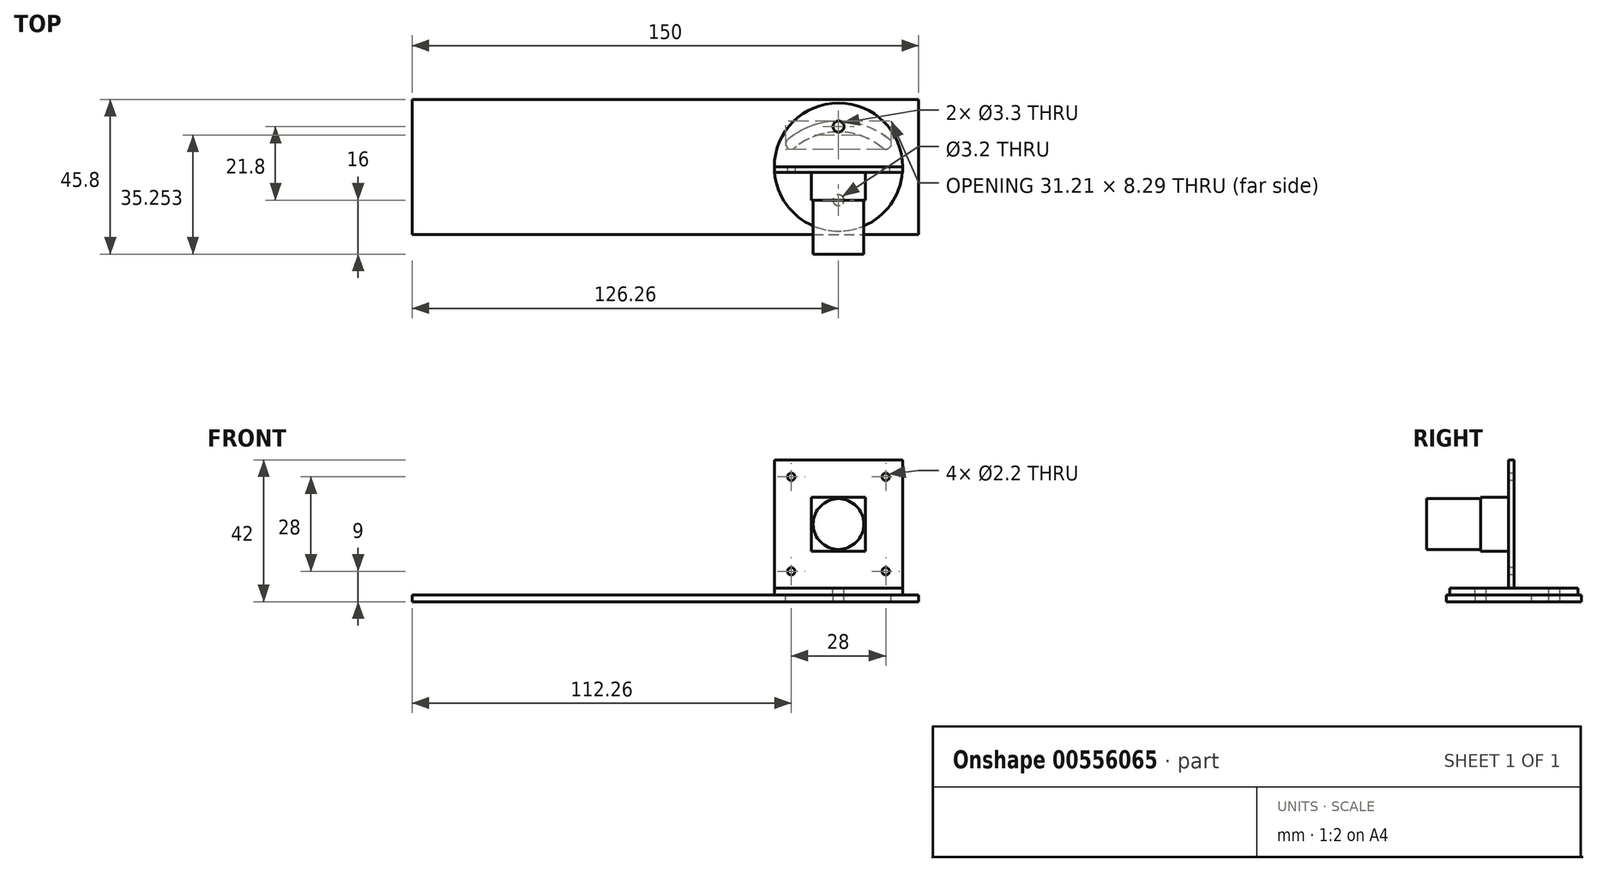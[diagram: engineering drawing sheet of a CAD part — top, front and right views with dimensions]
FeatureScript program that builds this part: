
annotation { "Feature Type Name" : "Feature", "Feature Type Description" : "" }
export const myFeature = defineFeature(function(context is Context, id is Id, definition is map)
    precondition{}
    {
        {
            var Q0;
            Q0=qCreatedBy(makeId("Front.planeOp"),FACE);
            var sketch = newSketch(context, id + "F0", { "sketchPlane" : qUnion([Q0])});
            skLineSegment(sketch, "E0.bottom", {"start": v(19, -19) * mm, "end": v(-19, -19) * mm});
            skLineSegment(sketch, "E0.top", {"start": v(19, 19) * mm, "end": v(-19, 19) * mm});
            skLineSegment(sketch, "E0.left", {"start": v(19, -19) * mm, "end": v(19, 19) * mm});
            skLineSegment(sketch, "E0.right", {"start": v(-19, -19) * mm, "end": v(-19, 19) * mm});
            skPoint(sketch, "E0.middle", {"position": v(0, 0) * mm});
            skSolve(sketch);
        }
        {
            var Q0;
            Q0 = qSketchRegion(id + "F0", true);
            extrude(context, id + "F1", {"entities" : qUnion([Q0]), "depth" : 1.6 * mm, "offsetDistance" : 25 * mm});
        }
        {
            var Q0;
            Q0=makeQuery(id+"F1.opExtrude","CAP_FACE",FACE,{"disambiguationData":[OSD([sQuery(id+"F0.wireOp",EDGE,"E0.bottom"),sQuery(id+"F0.wireOp",EDGE,"E0.top"),sQuery(id+"F0.wireOp",EDGE,"E0.left"),sQuery(id+"F0.wireOp",EDGE,"E0.right")])],"isStart":false});
            var sketch = newSketch(context, id + "F2", { "sketchPlane" : qUnion([Q0])});
            skLineSegment(sketch, "E1.bottom", {"start": v(14, -14) * mm, "end": v(-14, -14) * mm, "construction": true});
            skLineSegment(sketch, "E1.top", {"start": v(14, 14) * mm, "end": v(-14, 14) * mm, "construction": true});
            skLineSegment(sketch, "E1.left", {"start": v(14, -14) * mm, "end": v(14, 14) * mm, "construction": true});
            skLineSegment(sketch, "E1.right", {"start": v(-14, -14) * mm, "end": v(-14, 14) * mm, "construction": true});
            skPoint(sketch, "E1.middle", {"position": v(0, 0) * mm});
            skCircle(sketch, "E2", {"center": v(-14, 14) * mm, "radius": 1.1 * mm});
            skLineSegment(sketch, "E3", {"start": v(0, 19) * mm, "end": v(0, -19) * mm, "construction": true});
            skLineSegment(sketch, "E4", {"start": v(-19, 0) * mm, "end": v(19, 0) * mm, "construction": true});
            skCircle(sketch, "E5.MirrorC", {"center": v(14, 14) * mm, "radius": 1.1 * mm});
            skCircle(sketch, "E6.MirrorC", {"center": v(-14, -14) * mm, "radius": 1.1 * mm});
            skCircle(sketch, "E7.MirrorC", {"center": v(14, -14) * mm, "radius": 1.1 * mm});
            skSolve(sketch);
        }
        {
            var Q0;
            Q0 = qSketchRegion(id + "F2", true);
            var Q1;
            Q1=makeQuery(id+"F1.opExtrude","CAP_FACE",FACE,{"disambiguationData":[OSD([sQuery(id+"F0.wireOp",EDGE,"E0.bottom"),sQuery(id+"F0.wireOp",EDGE,"E0.top"),sQuery(id+"F0.wireOp",EDGE,"E0.left"),sQuery(id+"F0.wireOp",EDGE,"E0.right")])],"isStart":true});
            extrude(context, id + "F3", {"entities" : qUnion([Q0]), "operationType" : NewBodyOperationType.REMOVE, "endBound" : BoundingType.UP_TO_SURFACE, "oppositeDirection" : true, "depth" : 25 * mm, "endBoundEntityFace" : qUnion([Q1]), "offsetDistance" : 25 * mm});
        }
        {
            var Q0;
            Q0=makeQuery(id+"F1.opExtrude","CAP_FACE",FACE,{"disambiguationData":[OSD([sQuery(id+"F0.wireOp",EDGE,"E0.bottom"),sQuery(id+"F0.wireOp",EDGE,"E0.top"),sQuery(id+"F0.wireOp",EDGE,"E0.left"),sQuery(id+"F0.wireOp",EDGE,"E0.right")])],"isStart":false});
            var sketch = newSketch(context, id + "F4", { "sketchPlane" : qUnion([Q0])});
            skLineSegment(sketch, "E8.bottom", {"start": v(8, -8) * mm, "end": v(-8, -8) * mm});
            skLineSegment(sketch, "E8.top", {"start": v(8, 8) * mm, "end": v(-8, 8) * mm});
            skLineSegment(sketch, "E8.left", {"start": v(8, -8) * mm, "end": v(8, 8) * mm});
            skLineSegment(sketch, "E8.right", {"start": v(-8, -8) * mm, "end": v(-8, 8) * mm});
            skPoint(sketch, "E8.middle", {"position": v(0, 0) * mm});
            skSolve(sketch);
        }
        {
            var Q0;
            Q0 = qSketchRegion(id + "F4", true);
            extrude(context, id + "F5", {"entities" : qUnion([Q0]), "operationType" : NewBodyOperationType.ADD, "depth" : 8.2 * mm, "offsetDistance" : 25 * mm});
        }
        {
            var Q0;
            Q0=makeQuery(id+"F5.opExtrude","CAP_FACE",FACE,{"disambiguationData":[OSD([sQuery(id+"F4.wireOp",EDGE,"E8.bottom"),sQuery(id+"F4.wireOp",EDGE,"E8.top"),sQuery(id+"F4.wireOp",EDGE,"E8.left"),sQuery(id+"F4.wireOp",EDGE,"E8.right")])],"isStart":false});
            var sketch = newSketch(context, id + "F6", { "sketchPlane" : qUnion([Q0])});
            skLineSegment(sketch, "E9", {"start": v(0, 8) * mm, "end": v(0, -8) * mm, "construction": true});
            skLineSegment(sketch, "E10", {"start": v(-8, 0) * mm, "end": v(8, 0) * mm, "construction": true});
            skCircle(sketch, "E11", {"center": v(0, 0) * mm, "radius": 7.5 * mm});
            skSolve(sketch);
        }
        {
            var Q0;
            Q0 = qSketchRegion(id + "F6", true);
            extrude(context, id + "F7", {"entities" : qUnion([Q0]), "operationType" : NewBodyOperationType.ADD, "depth" : 16 * mm, "offsetDistance" : 25 * mm});
        }
        {
            var Q0;
            Q0=makeQuery(id+"F1.opExtrude","SWEPT_FACE",FACE,{"disambiguationData":[OSD([sQuery(id+"F0.wireOp",EDGE,"E0.bottom")])]});
            var sketch = newSketch(context, id + "F8", { "sketchPlane" : qUnion([Q0])});
            skCircle(sketch, "E12", {"center": v(0, 0) * mm, "radius": 19 * mm});
            skCircle(sketch, "E13", {"center": v(0, 9.8) * mm, "radius": 1.65 * mm});
            skLineSegment(sketch, "E14", {"start": v(0, 19) * mm, "end": v(0, -19) * mm, "construction": true});
            skCircle(sketch, "E15", {"center": v(0, -12) * mm, "radius": 1.65 * mm});
            skSolve(sketch);
        }
        {
            var Q0;
            Q0 = qSketchRegion(id + "F8", true);
            extrude(context, id + "F9", {"entities" : qUnion([Q0]), "depth" : 2 * mm, "offsetDistance" : 25 * mm});
        }
        {
            var Q0;
            Q0=makeQuery(id+"F9.opExtrude","SWEPT_BODY",BODY,{"disambiguationData":[OSD([sQuery(id+"F8.wireOp",EDGE,"E12"),sQuery(id+"F8.wireOp",EDGE,"E13"),sQuery(id+"F8.wireOp",EDGE,"E15")])]});
            transform(context, id + "F10", {"entities" : qUnion([Q0]), "transformType" : TransformType.TRANSLATION_3D, "dx" : 0 * mm, "dy" : 0 * mm, "dz" : 0 * mm, "makeCopy" : true});
        }
        {
            var Q0;
            Q0=makeQuery(id+"F10.opPattern","COPY",BODY,{"derivedFrom":makeQuery(id+"F9.opExtrude","SWEPT_BODY",BODY,{"disambiguationData":[OSD([sQuery(id+"F8.wireOp",EDGE,"E12"),sQuery(id+"F8.wireOp",EDGE,"E13"),sQuery(id+"F8.wireOp",EDGE,"E15")])]}),"instanceName":"1"});
            deleteBodies(context, id + "F11", {"entities" : qUnion([Q0])});
        }
        {
            var Q0;
            Q0=makeQuery(id+"F9.opExtrude","CAP_FACE",FACE,{"disambiguationData":[OSD([sQuery(id+"F8.wireOp",EDGE,"E12"),sQuery(id+"F8.wireOp",EDGE,"E13"),sQuery(id+"F8.wireOp",EDGE,"E15")])],"isStart":false});
            var sketch = newSketch(context, id + "F12", { "sketchPlane" : qUnion([Q0])});
            skLineSegment(sketch, "E16.bottom", {"start": v(-126.26, -20) * mm, "end": v(23.74, -20) * mm});
            skLineSegment(sketch, "E16.top", {"start": v(-126.26, 20) * mm, "end": v(23.74, 20) * mm});
            skLineSegment(sketch, "E16.left", {"start": v(-126.26, -20) * mm, "end": v(-126.26, 20) * mm});
            skLineSegment(sketch, "E16.right", {"start": v(23.74, -20) * mm, "end": v(23.74, 20) * mm});
            skLineSegment(sketch, "E17", {"start": v(23.74, 0) * mm, "end": v(-126.26, 0) * mm, "construction": true});
            skSolve(sketch);
        }
        {
            var Q0;
            Q0 = qSketchRegion(id + "F12", true);
            extrude(context, id + "F13", {"entities" : qUnion([Q0]), "depth" : 2 * mm, "offsetDistance" : 25 * mm});
        }
        {
            var Q0;
            Q0=makeQuery(id+"F13.opExtrude","CAP_FACE",FACE,{"disambiguationData":[OSD([sQuery(id+"F12.wireOp",EDGE,"E16.bottom"),sQuery(id+"F12.wireOp",EDGE,"E16.top"),sQuery(id+"F12.wireOp",EDGE,"E16.left"),sQuery(id+"F12.wireOp",EDGE,"E16.right")])],"isStart":true});
            var sketch = newSketch(context, id + "F14", { "sketchPlane" : qUnion([Q0])});
            skCircle(sketch, "E18", {"center": v(0, -9.8) * mm, "radius": 1.6 * mm});
            skCircle(sketch, "E19", {"center": v(0, -9.8) * mm, "radius": 21.8 * mm, "construction": true});
            skArc(sketch, "E20", {"start": v(-15.04, 8.13) * mm, "mid": v(-15.24, 5.87) * mm, "end": v(-12.98, 5.67) * mm});
            skArc(sketch, "E21", {"start": v(0, 13.6) * mm, "mid": v(-8, 12.19) * mm, "end": v(-15.04, 8.13) * mm});
            skArc(sketch, "E22", {"start": v(0, 10.4) * mm, "mid": v(-6.9, 9.18) * mm, "end": v(-12.98, 5.67) * mm});
            skLineSegment(sketch, "E23", {"start": v(-12.98, 5.67) * mm, "end": v(-15.04, 8.13) * mm, "construction": true});
            skLineSegment(sketch, "E24", {"start": v(-15.24, 5.87) * mm, "end": v(-14.01, 6.9) * mm, "construction": true});
            skLineSegment(sketch, "E25", {"start": v(-15.04, 8.13) * mm, "end": v(-15.04, 8.13) * mm});
            skLineSegment(sketch, "E26", {"start": v(-12.98, 5.67) * mm, "end": v(-12.98, 5.67) * mm});
            skLineSegment(sketch, "E27", {"start": v(0, -9.8) * mm, "end": v(0, 12) * mm, "construction": true});
            skArc(sketch, "E28.MirrorCS", {"start": v(0, 10.4) * mm, "mid": v(6.9, 9.18) * mm, "end": v(12.98, 5.67) * mm});
            skArc(sketch, "E29.MirrorCS", {"start": v(15.04, 8.13) * mm, "mid": v(15.24, 5.87) * mm, "end": v(12.98, 5.67) * mm});
            skArc(sketch, "E30.MirrorCS", {"start": v(0, 13.6) * mm, "mid": v(8, 12.19) * mm, "end": v(15.04, 8.13) * mm});
            skSolve(sketch);
        }
        {
            var Q0;
            Q0 = qSketchRegion(id + "F14", true);
            var Q1;
            Q1=makeQuery(id+"F13.opExtrude","CAP_FACE",FACE,{"disambiguationData":[OSD([sQuery(id+"F12.wireOp",EDGE,"E16.bottom"),sQuery(id+"F12.wireOp",EDGE,"E16.top"),sQuery(id+"F12.wireOp",EDGE,"E16.left"),sQuery(id+"F12.wireOp",EDGE,"E16.right")])],"isStart":false});
            extrude(context, id + "F15", {"entities" : qUnion([Q0]), "operationType" : NewBodyOperationType.REMOVE, "endBound" : BoundingType.UP_TO_SURFACE, "oppositeDirection" : true, "depth" : 25 * mm, "endBoundEntityFace" : qUnion([Q1]), "offsetDistance" : 25 * mm});
        }
    });
